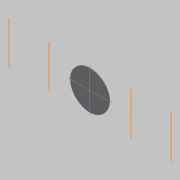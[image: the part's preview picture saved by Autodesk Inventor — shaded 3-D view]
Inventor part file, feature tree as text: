
AUTODESK INVENTOR PART (.ipt)
format: ipt  version: 2017.3 (Build 213257000, 257)  size: 223,744 bytes
history: native  units: in
note: dims shown in document units (in); Inventor stores cm internally (conversion verified against a paired STEP export)
features: other x13, extrude x3, sketch x2, split x2, hole x1
ambient origin geometry x8: Origin, YZ Plane, XZ Plane, XY Plane, X Axis, Y Axis, Z Axis, Center Point
bodies: Solid1 (feature_tree), Solid2 (feature_tree), Solid3 (feature_tree)
feature tree (21):
  other  "Centerline at Trunk OD"
  other  "Centerline at Repad OD"
  other  "Offset at Repad OD"
  other  "Bottom quadrant line - right"
  other  "Right quadrant line"
  other  "Bottom quadrant line - left"
  other  "Left quadrant line"
  other  "Top quadrant line"
  other  "Centerline at centerline"
  sketch  "Sketch1"  dims[d0=-0.0in d1=-0.0in]
  extrude  "Extrusion1"  [1 undecoded]
  split  "Split1"
  split  "Split2"
  hole  "Hole1"  [1 undecoded]
  other  "2D Equation Curve1"
  other  "2D Equation Curve2"
  other  "Srf1"
  other  "Srf2"
  sketch  "Sketch3"  dims[d2=0.0in d3=54.9779in d4=27.4889in d5=-54.9779in d6=-27.4889in d7=0.0in d8=0.0in d9=0.0in d10=141.7323in d11=0.0in d12=141.7323in d14=7.0001in d15=7.0001in d25=5.9999in d26=0.5in d27=0.0in d28=0.5in d29=0.0in d30=0.5in d31=0.0in d32=6.0in d36=0.422in d37=0.339in d38=0.0246in d39=0.426in d40=0.375in d41=0.25in d42=0.5635in d43=1.0in d44=0.8108in d45=12.0in]
  extrude  "ExtrusionSrf1"  Depth=27.4889in
  extrude  "ExtrusionSrf2"  [1 undecoded]
note: 3 required parameter values undecoded (feature->parameter linkage not recoverable at this tier; creation-order binding heuristic only, values carry confidence <= 0.55)
